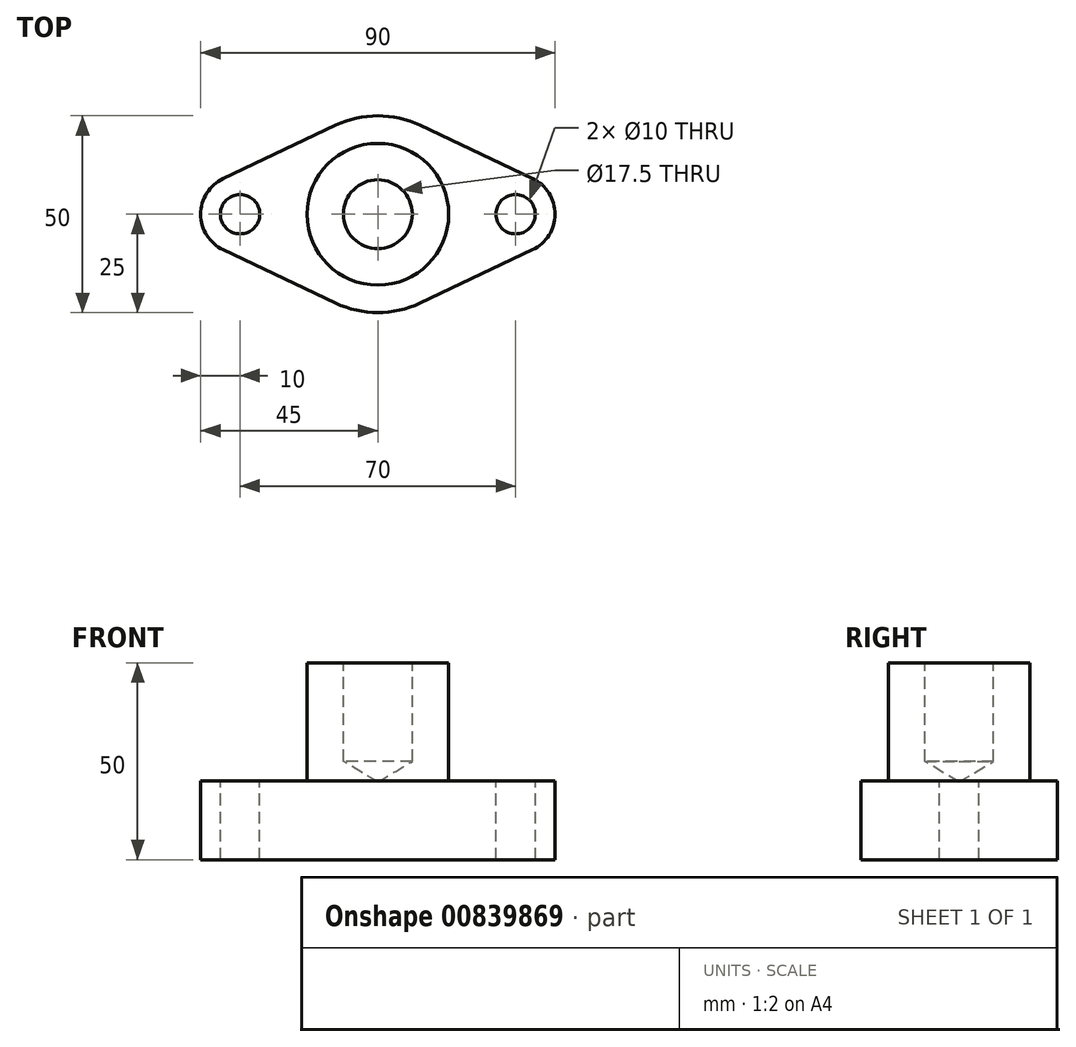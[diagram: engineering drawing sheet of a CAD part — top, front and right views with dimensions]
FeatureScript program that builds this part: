
annotation { "Feature Type Name" : "Feature", "Feature Type Description" : "" }
export const myFeature = defineFeature(function(context is Context, id is Id, definition is map)
    precondition{}
    {
        {
            var Q0;
            Q0=qCreatedBy(makeId("Top.planeOp"),FACE);
            var sketch = newSketch(context, id + "F0", { "sketchPlane" : qUnion([Q0])});
            skLineSegment(sketch, "E0", {"start": v(0, 0) * mm, "end": v(35, 0) * mm});
            skLineSegment(sketch, "E1", {"start": v(0, 0) * mm, "end": v(-35, 0) * mm});
            skArc(sketch, "E2", {"start": v(-10.71, -22.59) * mm, "mid": v(0, -25) * mm, "end": v(10.71, -22.59) * mm});
            skArc(sketch, "E3", {"start": v(-39.29, 9.04) * mm, "mid": v(-45, 0) * mm, "end": v(-39.29, -9.04) * mm});
            skArc(sketch, "E4", {"start": v(39.29, -9.04) * mm, "mid": v(45, 0) * mm, "end": v(39.29, 9.04) * mm});
            skLineSegment(sketch, "E5", {"start": v(-10.71, 22.59) * mm, "end": v(-39.29, 9.04) * mm});
            skLineSegment(sketch, "E6", {"start": v(-10.71, -22.59) * mm, "end": v(-39.29, -9.04) * mm});
            skLineSegment(sketch, "E7", {"start": v(10.71, 22.59) * mm, "end": v(39.29, 9.04) * mm});
            skPoint(sketch, "E8.orphan", {"position": v(0, 27.67) * mm});
            skLineSegment(sketch, "E9", {"start": v(10.71, -22.59) * mm, "end": v(39.29, -9.04) * mm});
            skArc(sketch, "E10.trimOffspring", {"start": v(10.71, 22.59) * mm, "mid": v(0, 25) * mm, "end": v(-10.71, 22.59) * mm});
            skSolve(sketch);
        }
        {
            var Q0;
            Q0=makeQuery(id+"F0.imprint","IMPRINT",FACE,{"disambiguationData":[TD([[makeQuery(id+"F0.imprint","IMPRINT",EDGE,{"derivedFrom":sQuery(id+"F0.wireOp",EDGE,"E2")}),1.0]])]});
            extrude(context, id + "F1", {"entities" : qUnion([Q0]), "depth" : 20 * mm, "offsetDistance" : 25 * mm});
        }
        {
            var Q0;
            Q0=makeQuery(id+"F1.opExtrude","CAP_FACE",FACE,{"disambiguationData":[OSD([sQuery(id+"F0.wireOp",EDGE,"E2"),sQuery(id+"F0.wireOp",EDGE,"E3"),sQuery(id+"F0.wireOp",EDGE,"E4"),sQuery(id+"F0.wireOp",EDGE,"E5"),sQuery(id+"F0.wireOp",EDGE,"E6"),sQuery(id+"F0.wireOp",EDGE,"E7"),sQuery(id+"F0.wireOp",EDGE,"E9"),sQuery(id+"F0.wireOp",EDGE,"E10.trimOffspring")])],"isStart":false});
            var sketch = newSketch(context, id + "F2", { "sketchPlane" : qUnion([Q0])});
            skLineSegment(sketch, "E11", {"start": v(0, 0) * mm, "end": v(-35, 0) * mm});
            skLineSegment(sketch, "E12", {"start": v(0, 0) * mm, "end": v(35, 0) * mm});
            skSolve(sketch);
        }
        {
            var Q0;
            Q0=sQuery(id+"F2.wireOp",VERTEX,"E11.end");
            var Q1;
            Q1=sQuery(id+"F2.wireOp",VERTEX,"E12.end");
            var Q2;
            Q2=makeQuery(id+"F1.opExtrude","SWEPT_BODY",BODY,{"disambiguationData":[OSD([sQuery(id+"F0.wireOp",EDGE,"E2"),sQuery(id+"F0.wireOp",EDGE,"E3"),sQuery(id+"F0.wireOp",EDGE,"E4"),sQuery(id+"F0.wireOp",EDGE,"E5"),sQuery(id+"F0.wireOp",EDGE,"E6"),sQuery(id+"F0.wireOp",EDGE,"E7"),sQuery(id+"F0.wireOp",EDGE,"E9"),sQuery(id+"F0.wireOp",EDGE,"E10.trimOffspring")])]});
            hole(context, id + "F3", {"style" : HoleStyle.SIMPLE, "endStyle" : HoleEndStyle.BLIND, "holeDiameter" : 10 * mm, "majorDiameter" : 5 * mm, "holeDepth" : 102 * mm, "isTappedThrough" : true, "tappedDepth" : 12 * mm, "tapClearance" : 3, "locations" : qUnion([Q0, Q1]), "scope" : qUnion([Q2])});
        }
        {
            var Q0;
            Q0=makeQuery(id+"F1.opExtrude","CAP_FACE",FACE,{"disambiguationData":[OSD([sQuery(id+"F0.wireOp",EDGE,"E2"),sQuery(id+"F0.wireOp",EDGE,"E3"),sQuery(id+"F0.wireOp",EDGE,"E4"),sQuery(id+"F0.wireOp",EDGE,"E5"),sQuery(id+"F0.wireOp",EDGE,"E6"),sQuery(id+"F0.wireOp",EDGE,"E7"),sQuery(id+"F0.wireOp",EDGE,"E9"),sQuery(id+"F0.wireOp",EDGE,"E10.trimOffspring")])],"isStart":false});
            var sketch = newSketch(context, id + "F4", { "sketchPlane" : qUnion([Q0])});
            skCircle(sketch, "E13", {"center": v(0, 0) * mm, "radius": 18 * mm});
            skSolve(sketch);
        }
        {
            var Q0;
            Q0=makeQuery(id+"F4.imprint","IMPRINT",FACE,{"disambiguationData":[TD([[makeQuery(id+"F4.imprint","IMPRINT",EDGE,{"derivedFrom":sQuery(id+"F4.wireOp",EDGE,"E13")}),1.0]])]});
            extrude(context, id + "F5", {"entities" : qUnion([Q0]), "operationType" : NewBodyOperationType.ADD, "depth" : 30 * mm, "offsetDistance" : 25 * mm});
        }
        {
            var Q0;
            Q0=makeQuery(id+"F5.opExtrude","CAP_FACE",FACE,{"disambiguationData":[OSD([sQuery(id+"F4.wireOp",EDGE,"E13")])],"isStart":false});
            var sketch = newSketch(context, id + "F6", { "sketchPlane" : qUnion([Q0])});
            skLineSegment(sketch, "E14", {"start": v(0, 0) * mm, "end": v(0, -18) * mm});
            skSolve(sketch);
        }
        {
            var Q0;
            Q0=sQuery(id+"F6.wireOp",VERTEX,"E14.start");
            var Q1;
            Q1=makeQuery(id+"F1.opExtrude","SWEPT_BODY",BODY,{"disambiguationData":[OSD([sQuery(id+"F0.wireOp",EDGE,"E2"),sQuery(id+"F0.wireOp",EDGE,"E3"),sQuery(id+"F0.wireOp",EDGE,"E4"),sQuery(id+"F0.wireOp",EDGE,"E5"),sQuery(id+"F0.wireOp",EDGE,"E6"),sQuery(id+"F0.wireOp",EDGE,"E7"),sQuery(id+"F0.wireOp",EDGE,"E9"),sQuery(id+"F0.wireOp",EDGE,"E10.trimOffspring")])]});
            hole(context, id + "F7", {"style" : HoleStyle.SIMPLE, "endStyle" : HoleEndStyle.BLIND, "standardTappedOrClearance" : lookupTablePath({ "fit" : "Normal", "standard" : "ISO", "size" : "M16", "type" : "Clearance" }), "standardBlindInLast" : lookupTablePath({ "fit" : "Standard", "standard" : "ISO", "size" : "M16", "type" : "Clearance" }), "holeDiameter" : 17.5 * mm, "majorDiameter" : 5 * mm, "holeDepth" : 25 * mm, "isTappedThrough" : true, "tappedDepth" : 12 * mm, "tapClearance" : 3, "locations" : qUnion([Q0]), "scope" : qUnion([Q1])});
        }
    });
